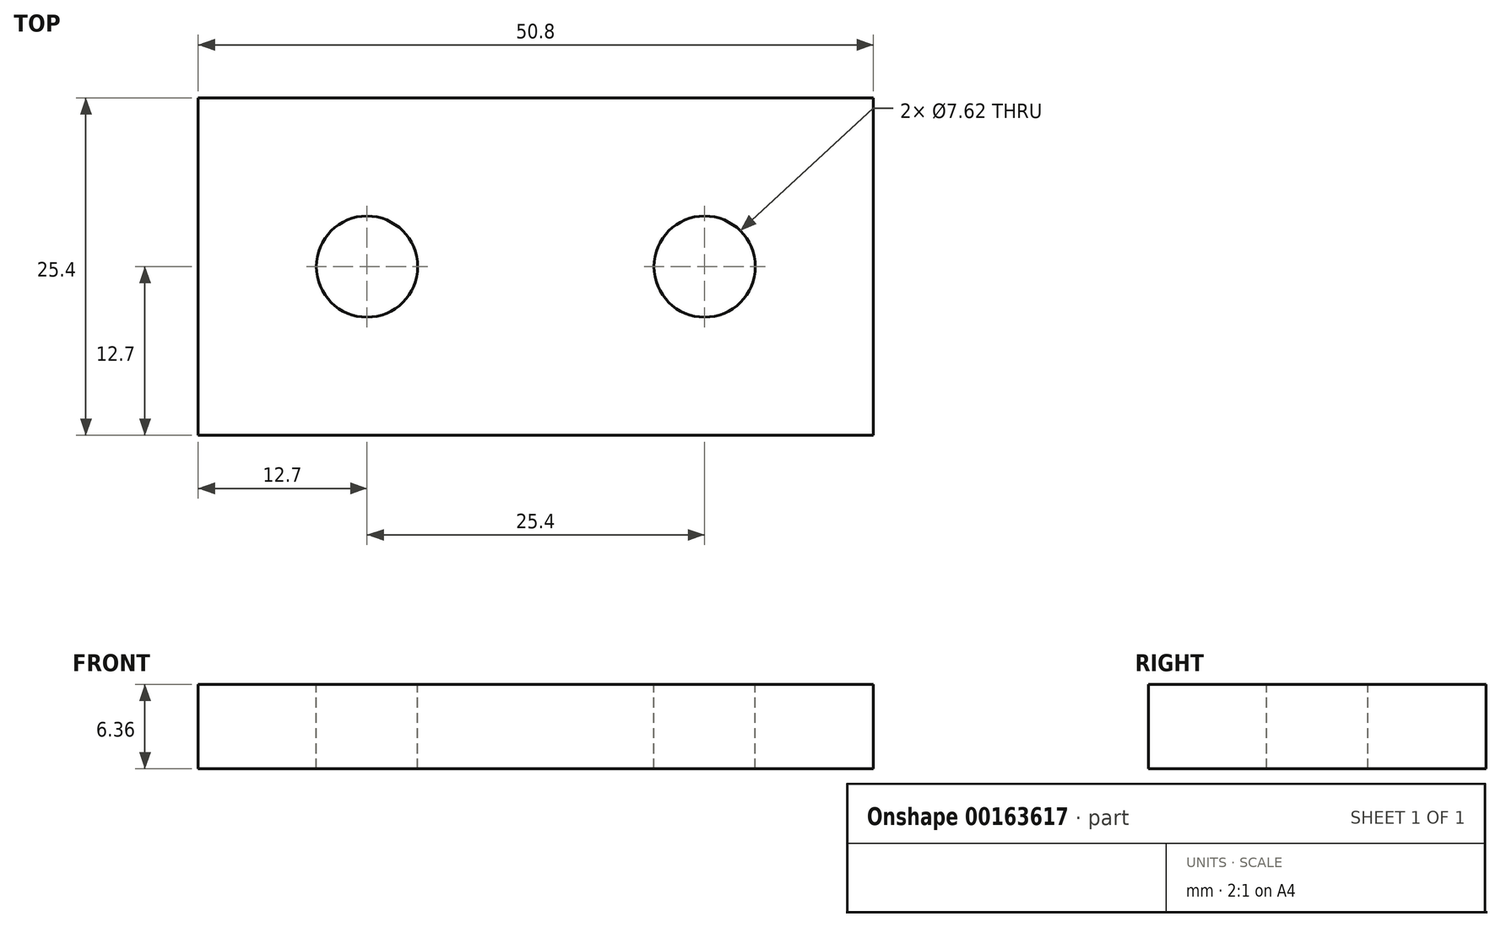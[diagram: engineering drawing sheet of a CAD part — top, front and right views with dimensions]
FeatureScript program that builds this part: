
annotation { "Feature Type Name" : "Feature", "Feature Type Description" : "" }
export const myFeature = defineFeature(function(context is Context, id is Id, definition is map)
    precondition{}
    {
        {
            var Q0;
            Q0=qCreatedBy(makeId("Top.planeOp"),FACE);
            var sketch = newSketch(context, id + "F0", { "sketchPlane" : qUnion([Q0])});
            skLineSegment(sketch, "E0.bottom", {"start": v(25.4, 12.7) * mm, "end": v(-25.4, 12.7) * mm});
            skLineSegment(sketch, "E0.top", {"start": v(25.4, -12.7) * mm, "end": v(-25.4, -12.7) * mm});
            skLineSegment(sketch, "E0.left", {"start": v(25.4, 12.7) * mm, "end": v(25.4, -12.7) * mm});
            skLineSegment(sketch, "E0.right", {"start": v(-25.4, 12.7) * mm, "end": v(-25.4, -12.7) * mm});
            skPoint(sketch, "E0.middle", {"position": v(0, 0) * mm});
            skSolve(sketch);
        }
        {
            var Q0;
            Q0 = qSketchRegion(id + "F0", true);
            extrude(context, id + "F1", {"entities" : qUnion([Q0]), "endBound" : BoundingType.SYMMETRIC, "depth" : 6.35 * mm});
        }
        {
            var Q0;
            Q0=makeQuery(id+"F1.opExtrude","CAP_FACE",FACE,{"disambiguationData":[OSD([sQuery(id+"F0.wireOp",EDGE,"E0.bottom"),sQuery(id+"F0.wireOp",EDGE,"E0.top"),sQuery(id+"F0.wireOp",EDGE,"E0.left"),sQuery(id+"F0.wireOp",EDGE,"E0.right")])],"isStart":false});
            var sketch = newSketch(context, id + "F2", { "sketchPlane" : qUnion([Q0])});
            skCircle(sketch, "E1", {"center": v(-12.7, 0) * mm, "radius": 3.81 * mm});
            skCircle(sketch, "E2", {"center": v(12.7, 0) * mm, "radius": 3.81 * mm});
            skLineSegment(sketch, "E3", {"start": v(-12.7, 0) * mm, "end": v(12.7, 0) * mm, "construction": true});
            skSolve(sketch);
        }
        {
            var Q0;
            Q0 = qSketchRegion(id + "F2", true);
            extrude(context, id + "F3", {"entities" : qUnion([Q0]), "operationType" : NewBodyOperationType.REMOVE, "oppositeDirection" : true, "depth" : 25.4 * mm});
        }
    });
